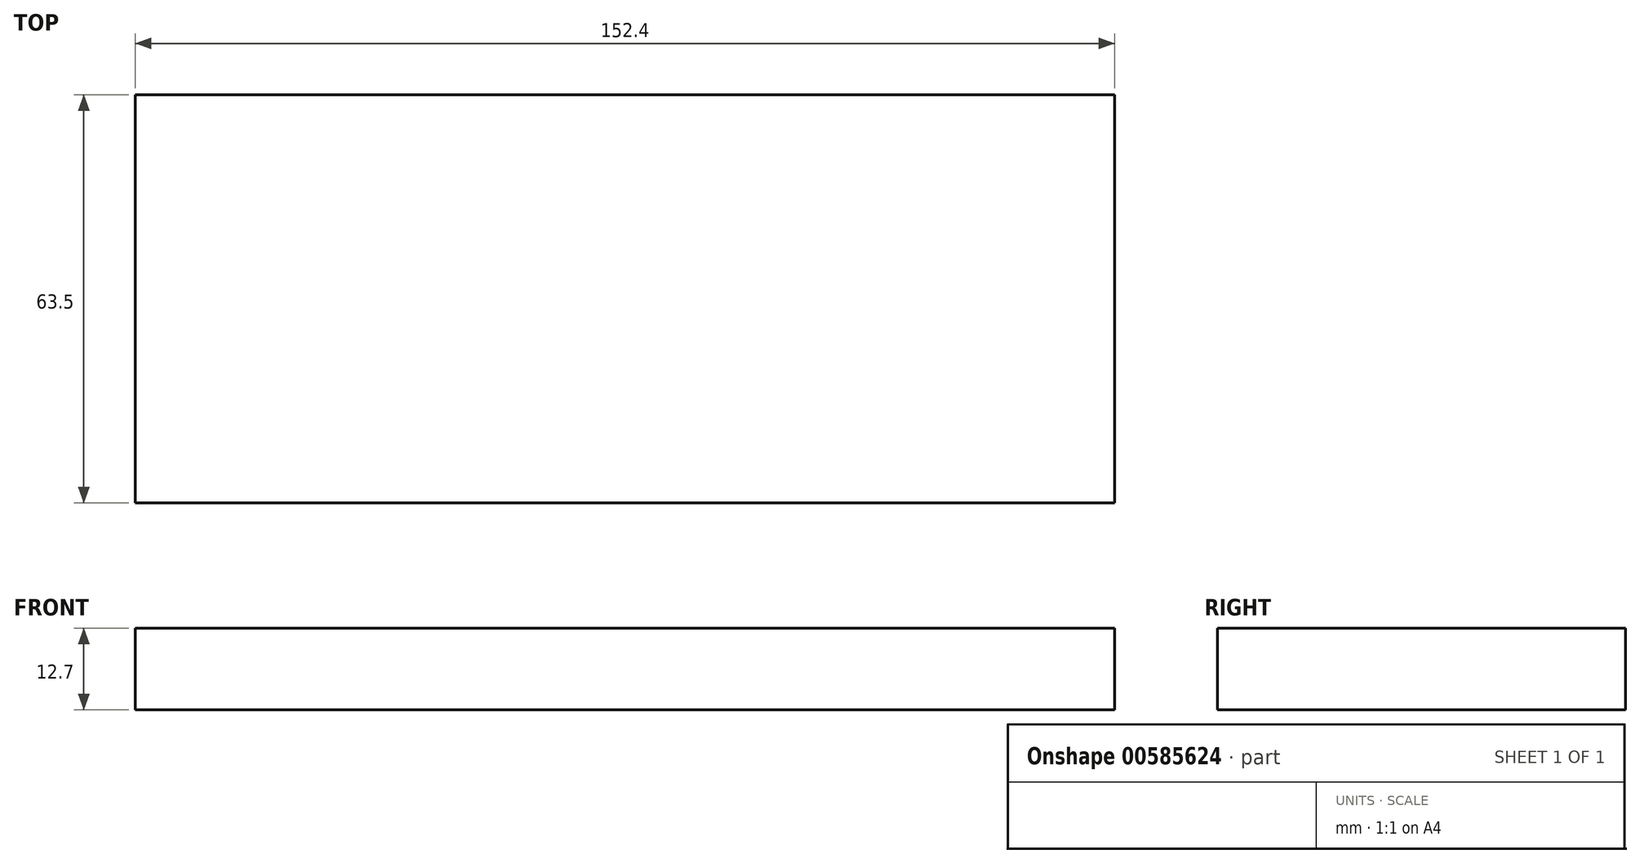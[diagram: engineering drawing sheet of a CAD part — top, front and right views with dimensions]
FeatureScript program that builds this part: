
annotation { "Feature Type Name" : "Feature", "Feature Type Description" : "" }
export const myFeature = defineFeature(function(context is Context, id is Id, definition is map)
    precondition{}
    {
        {
            var Q0;
            Q0=qCreatedBy(makeId("Top.planeOp"),FACE);
            var sketch = newSketch(context, id + "F0", { "sketchPlane" : qUnion([Q0])});
            skLineSegment(sketch, "E0.bottom", {"start": v(-76.2, 31.75) * mm, "end": v(76.2, 31.75) * mm});
            skLineSegment(sketch, "E0.top", {"start": v(-76.2, -31.75) * mm, "end": v(76.2, -31.75) * mm});
            skLineSegment(sketch, "E0.left", {"start": v(-76.2, 31.75) * mm, "end": v(-76.2, -31.75) * mm});
            skLineSegment(sketch, "E0.right", {"start": v(76.2, 31.75) * mm, "end": v(76.2, -31.75) * mm});
            skPoint(sketch, "E0.middle", {"position": v(0, 0) * mm});
            skSolve(sketch);
        }
        {
            var Q0;
            Q0=makeQuery(id+"F0.imprint","IMPRINT",FACE,{"disambiguationData":[TD([[makeQuery(id+"F0.imprint","IMPRINT",EDGE,{"derivedFrom":sQuery(id+"F0.wireOp",EDGE,"E0.bottom")}),-1.0]])]});
            extrude(context, id + "F1", {"entities" : qUnion([Q0]), "depth" : 12.7 * mm, "offsetDistance" : 25.4 * mm});
        }
    });
